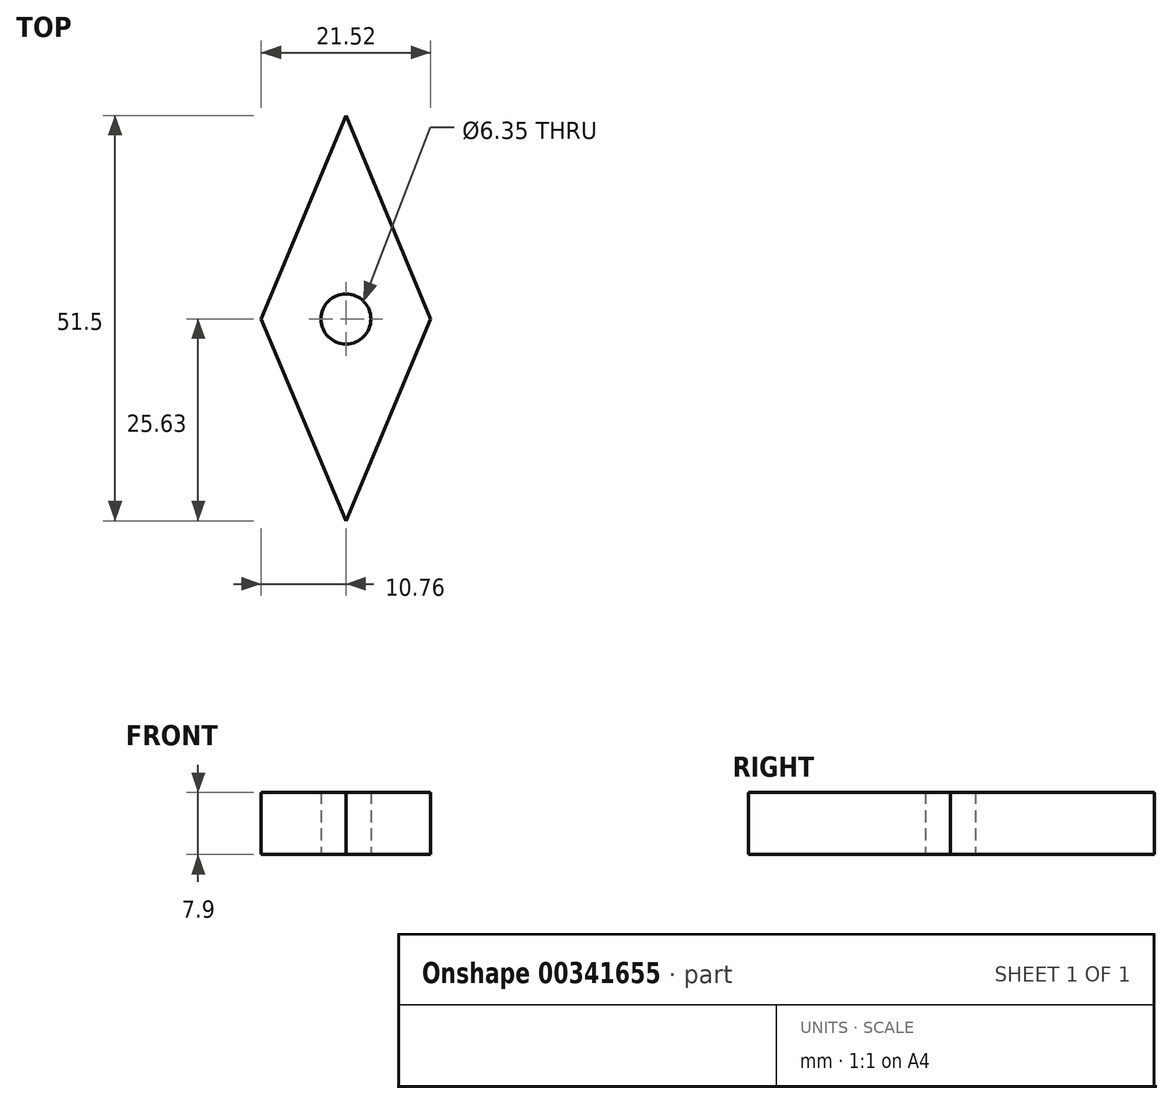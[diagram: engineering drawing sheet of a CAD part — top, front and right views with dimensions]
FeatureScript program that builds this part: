
annotation { "Feature Type Name" : "Feature", "Feature Type Description" : "" }
export const myFeature = defineFeature(function(context is Context, id is Id, definition is map)
    precondition{}
    {
        {
            var Q0;
            Q0=qCreatedBy(makeId("Top.planeOp"),FACE);
            var sketch = newSketch(context, id + "F0", { "sketchPlane" : qUnion([Q0])});
            skLineSegment(sketch, "E0", {"start": v(0, 0) * mm, "end": v(0, 25.87) * mm});
            skLineSegment(sketch, "E1", {"start": v(0, 25.87) * mm, "end": v(0, 0) * mm});
            skLineSegment(sketch, "E2", {"start": v(0, 0) * mm, "end": v(0, -25.63) * mm});
            skLineSegment(sketch, "E3", {"start": v(0, -25.63) * mm, "end": v(0, 0) * mm});
            skLineSegment(sketch, "E4", {"start": v(0, 0) * mm, "end": v(10.76, 0) * mm});
            skLineSegment(sketch, "E5", {"start": v(10.76, 0) * mm, "end": v(0, 0) * mm});
            skLineSegment(sketch, "E6", {"start": v(0, 0) * mm, "end": v(-10.76, 0) * mm});
            skLineSegment(sketch, "E7", {"start": v(-10.76, 0) * mm, "end": v(0, 0) * mm});
            skLineSegment(sketch, "E8", {"start": v(0, 25.87) * mm, "end": v(10.76, 0) * mm});
            skLineSegment(sketch, "E9", {"start": v(-10.76, 0) * mm, "end": v(0, 25.87) * mm});
            skLineSegment(sketch, "E10", {"start": v(-10.76, 0) * mm, "end": v(0, -25.63) * mm});
            skLineSegment(sketch, "E11", {"start": v(10.76, 0) * mm, "end": v(0, -25.63) * mm});
            skCircle(sketch, "E12", {"center": v(0, 0) * mm, "radius": 3.17 * mm});
            skSolve(sketch);
        }
        {
            var Q0;
            Q0 = qSketchRegion(id + "F0", true);
            extrude(context, id + "F1", {"entities" : qUnion([Q0]), "depth" : 7.9 * mm});
        }
    });
